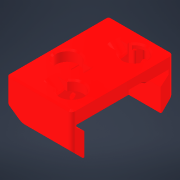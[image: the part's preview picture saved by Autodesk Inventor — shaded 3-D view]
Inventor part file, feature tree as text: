
AUTODESK INVENTOR PART (.ipt)
format: ipt  version: 2022.1 (Build 261234000, 234)  size: 1,927,680 bytes
history: native  units: mm
features: projected_geometry x28, sketch x23, extrude x21, reference x19, delete_face x18, chamfer x15, move_body x11, direct_edit x10, other x4, fillet x3, hole x2, plane x1
ambient origin geometry x8: Origin, YZ Plane, XZ Plane, XY Plane, X Axis, Y Axis, Z Axis, Center Point
bodies: Volumenkörper1 (feature_tree)
feature tree (155):
  delete_face  "Fläche löschen1"
  delete_face  "Fläche löschen2"
  delete_face  "Fläche löschen3"
  delete_face  "Fläche löschen4"
  delete_face  "Fläche löschen5"
  extrude  "Extrusion1"  TaperAngle=0.0deg  [1 undecoded]
  direct_edit  "Direktbearbeitung1"
  extrude  "Extrusion2"  Depth=3.4mm
  extrude  "Extrusion3"  Depth=3.4mm
  delete_face  "Fläche löschen10"
  direct_edit  "Direktbearbeitung2"
  sketch  "Skizze7"  dims[d10=0.1mm d11=0.15mm]
  plane  "Arbeitsebene1"
  extrude  "Extrusion4"  Depth=0.15mm
  delete_face  "Fläche löschen11"
  delete_face  "Fläche löschen12"
  extrude  "Extrusion5"  Depth=0.6mm
  extrude  "Extrusion6"  Depth=0.5mm
  chamfer  "Fase1"  Distance=0.6mm
  hole  "Bohrung1"  [1 undecoded]
  extrude  "Extrusion7"  Depth=0.1mm
  hole  "Bohrung2"  [1 undecoded]
  chamfer  "Fase2"  [1 undecoded]
  chamfer  "Fase3"  Distance=0.21mm
  chamfer  "Fase4"  Distance=2.0mm Angle=45.0deg
  extrude  "Extrusion8"  TaperAngle=0.0deg  [1 undecoded]
  extrude  "Extrusion9"  Depth=0.1mm
  chamfer  "Fase5"  Distance=1.0mm
  extrude  "Extrusion10"  Depth=2.0mm TaperAngle=45.0deg
  direct_edit  "Direktbearbeitung3"
  delete_face  "Fläche löschen13"
  direct_edit  "Direktbearbeitung5"
  extrude  "Extrusion11"  Depth=2.0mm TaperAngle=45.0deg
  delete_face  "Fläche löschen14"
  extrude  "Extrusion12"  Depth=2.0mm
  chamfer  "Fase6"  Distance=1.0mm
  direct_edit  "Direktbearbeitung6"
  direct_edit  "Direktbearbeitung7"
  direct_edit  "Direktbearbeitung8"
  extrude  "Extrusion13"  Depth=3.5mm
  chamfer  "Fase7"  [1 undecoded]
  fillet  "Rundung1"  Radius=0.42mm
  direct_edit  "Direktbearbeitung9"
  delete_face  "Fläche löschen15"
  delete_face  "Fläche löschen16"
  chamfer  "Fase8"  Distance=2.0mm
  delete_face  "Fläche löschen17"
  delete_face  "Fläche löschen18"
  delete_face  "Fläche löschen19"
  extrude  "Extrusion14"  Depth=2.0mm
  extrude  "Extrusion15"  Depth=5.0mm
  extrude  "Extrusion16"  TaperAngle=0.0deg  [1 undecoded]
  chamfer  "Fase9"  Distance=0.3mm
  chamfer  "Fase10"  Distance=0.5mm
  direct_edit  "Direktbearbeitung10"
  extrude  "Extrusion17"  Depth=2.0mm
  chamfer  "Fase11"  [1 undecoded]
  chamfer  "Fase12"  Distance=2.0mm
  fillet  "Rundung3"  Radius=2.0mm
  extrude  "Extrusion18"  Depth=2.0mm
  fillet  "Rundung4"  Radius=0.41mm
  delete_face  "Fläche löschen20"
  delete_face  "Fläche löschen21"
  delete_face  "Fläche löschen22"
  direct_edit  "Direktbearbeitung11"
  chamfer  "Fase13"  Distance=0.2mm
  extrude  "Extrusion19"  Depth=2.0mm TaperAngle=45.0deg
  chamfer  "Fase14"  [1 undecoded]
  extrude  "Extrusion20"  Depth=2.0mm TaperAngle=0.0deg
  extrude  "Extrusion21"  TaperAngle=0.0deg  [1 undecoded]
  chamfer  "Fase15"  [1 undecoded]
  sketch  "Skizze1"  dims[d0=0.0mm d1=0.0mm d2=0.0mm d3=0.0mm d4=-0.2mm]
  projected_geometry  "Projizierte Kontur1"
  reference  "Referenz1"
  reference  "Referenz2"
  sketch  "Skizze2"  dims[d5=4.165mm d6=3.4mm]
  reference  "Referenz3"
  sketch  "Skizze6"  dims[d7=4.165mm d8=3.4mm]
  projected_geometry  "Projizierte Kontur11"
  projected_geometry  "Projizierte Kontur12"
  projected_geometry  "Projizierte Kontur13"
  projected_geometry  "Projizierte Kontur14"
  projected_geometry  "Projizierte Kontur15"
  reference  "Referenz7"
  projected_geometry  "Projizierte Kontur16"
  projected_geometry  "Projizierte Kontur17"
  sketch  "Skizze8"  dims[d12=0.1mm d13=0.6mm]
  projected_geometry  "Projizierte Kontur18"
  projected_geometry  "Projizierte Kontur19"
  sketch  "Skizze9"  dims[d14=0.5mm d15=0.5mm d16=0.6mm d17=0.0mm]
  projected_geometry  "Projizierte Kontur20"
  sketch  "Skizze10"  dims[d18=3.25mm d19=0.006mm d20=0.0mm]
  reference  "Referenz8"
  reference  "Referenz9"
  sketch  "Skizze11"  dims[d21=0.0mm d22=0.0mm d23=0.05mm d24=0.1mm]
  reference  "Referenz10"
  reference  "Referenz11"
  reference  "Referenz12"
  reference  "Referenz13"
  reference  "Referenz14"
  reference  "Referenz15"
  projected_geometry  "Projizierte Kontur21"
  sketch  "Skizze12"  dims[d25=10.0mm d26=0.0mm d27=6.108652mm]
  reference  "Referenz16"
  reference  "Referenz17"
  sketch  "Skizze13"  dims[d28=0.4mm d29=0.0mm d30=0.0mm d31=0.21mm d32=0.0mm d33=0.21mm d34=2.0mm d35=45.0deg]
  reference  "Referenz18"
  reference  "Referenz19"
  projected_geometry  "Projizierte Kontur22"
  sketch  "Skizze14"  dims[d36=1.6mm d37=6.0mm d38=4.0mm d39=2.0mm d40=90.0deg d41=6.0mm d42=0.0mm d43=0.0mm]
  reference  "Referenz20"
  sketch  "Skizze15"  dims[d44=0.1mm d45=0.1mm]
  projected_geometry  "Projizierte Kontur23"
  sketch  "Skizze16"  dims[d46=0.15mm d47=1.0mm d48=0.0mm]
  projected_geometry  "Projizierte Kontur24"
  projected_geometry  "Projizierte Kontur25"
  sketch  "Skizze17"  dims[d49=4.0mm d50=6.0mm d51=4.4mm d52=2.3mm d53=90.0deg d54=6.0mm d55=0.0mm d56=0.4mm d57=2.0mm d58=45.0deg]
  projected_geometry  "Projizierte Kontur26"
  sketch  "Skizze18"  dims[d59=0.4mm d60=2.0mm d61=45.0deg d62=0.4mm d63=2.0mm d64=45.0deg]
  projected_geometry  "Projizierte Kontur27"
  sketch  "Skizze19"  dims[d65=1.0mm d66=2.0mm]
  projected_geometry  "Projizierte Kontur28"
  projected_geometry  "Projizierte Kontur29"
  reference  "Referenz21"
  reference  "Referenz22"
  sketch  "Skizze20"  dims[d67=0.2mm d68=1.0mm d69=0.0mm]
  projected_geometry  "Projizierte Kontur30"
  projected_geometry  "Projizierte Kontur31"
  sketch  "Skizze21"  dims[d70=0.7mm d71=3.5mm d72=0.0mm d73=0.0mm]
  projected_geometry  "Projizierte Kontur32"
  projected_geometry  "Projizierte Kontur33"
  sketch  "Skizze22"  dims[d74=0.2mm d75=2.0mm d76=45.0deg d77=0.42mm d78=2.0mm d79=0.0mm]
  projected_geometry  "Projizierte Kontur34"
  projected_geometry  "Projizierte Kontur35"
  sketch  "Skizze23"  dims[d80=0.0mm d81=0.0mm d82=0.4mm d83=2.0mm]
  sketch  "Skizze24"  dims[d84=1.0mm d85=5.0mm]
  sketch  "Skizze25"  dims[d86=1.0mm d90=0.0mm d91=0.0mm d92=-0.4mm]
  projected_geometry  "Projizierte Kontur36"
  sketch  "Skizze26"  dims[d93=0.3mm d94=0.3mm d95=0.5mm d96=0.5mm d97=0.0mm d98=0.0mm d99=2.0mm d100=2.0mm d101=3.0mm d102=0.41mm d103=0.2mm d104=0.0mm d105=0.2mm d106=2.0mm d107=45.0deg d108=0.0mm d109=0.0mm d110=-0.8mm d111=0.0mm d112=0.0mm d113=0.3mm d114=0.0mm d115=0.0mm d116=-0.75mm d117=0.0mm d118=0.0mm d119=-0.4mm d120=0.0mm d121=0.0mm d122=0.32309mm d123=2.0mm d124=45.0deg d125=1.0mm d126=0.0mm d127=0.0mm d128=0.4mm d129=0.6mm d130=2.0mm d131=45.0deg d132=8.0mm d133=0.0mm d134=0.8mm d135=0.0mm d136=0.0mm d137=0.0mm d138=1.8mm d139=2.0mm d140=8.726646mm d141=1.8mm d142=2.0mm d143=8.726646mm d144=0.0mm d145=0.0mm d146=0.05mm d147=2.4mm d148=0.0mm d149=0.3mm d150=2.0mm d151=8.726646mm d152=0.4mm d153=2.0mm d154=8.726646mm d156=0.5mm d157=135.0deg d158=45.0deg d159=0.4mm d160=0.4mm d161=0.0mm d162=0.0mm d163=1.0mm d164=0.0mm d165=0.0mm d166=-1.0mm d167=1.0mm d168=2.0mm d169=8.726646mm d170=10.0mm d171=0.0mm d172=0.2mm d173=2.0mm d174=8.726646mm d175=1.0mm d176=0.0mm d177=9.5mm d178=1.0mm d179=0.0mm d180=0.4mm d181=2.0mm d182=8.726646mm]
  projected_geometry  "Projizierte Kontur37"
  other  "Probe v0.2"
  other  "<userpath>\Desktop\Glicky\Assembly.iam"
  other  "Assembly.iam"
  other  "Glicky_3D:1"
  move_body  "Verschieben1"
  move_body  "Verschieben2"
  move_body  "Verschieben3"
  move_body  "Verschieben5"
  move_body  "Verschieben6"
  move_body  "Verschieben7"
  move_body  "Verschieben8"
  move_body  "Verschieben9"
  move_body  "Verschieben10"
  move_body  "Verschieben11"
  move_body  "Verschieben12"
note: 11 required parameter values undecoded (feature->parameter linkage not recoverable at this tier; creation-order binding heuristic only, values carry confidence <= 0.55)
